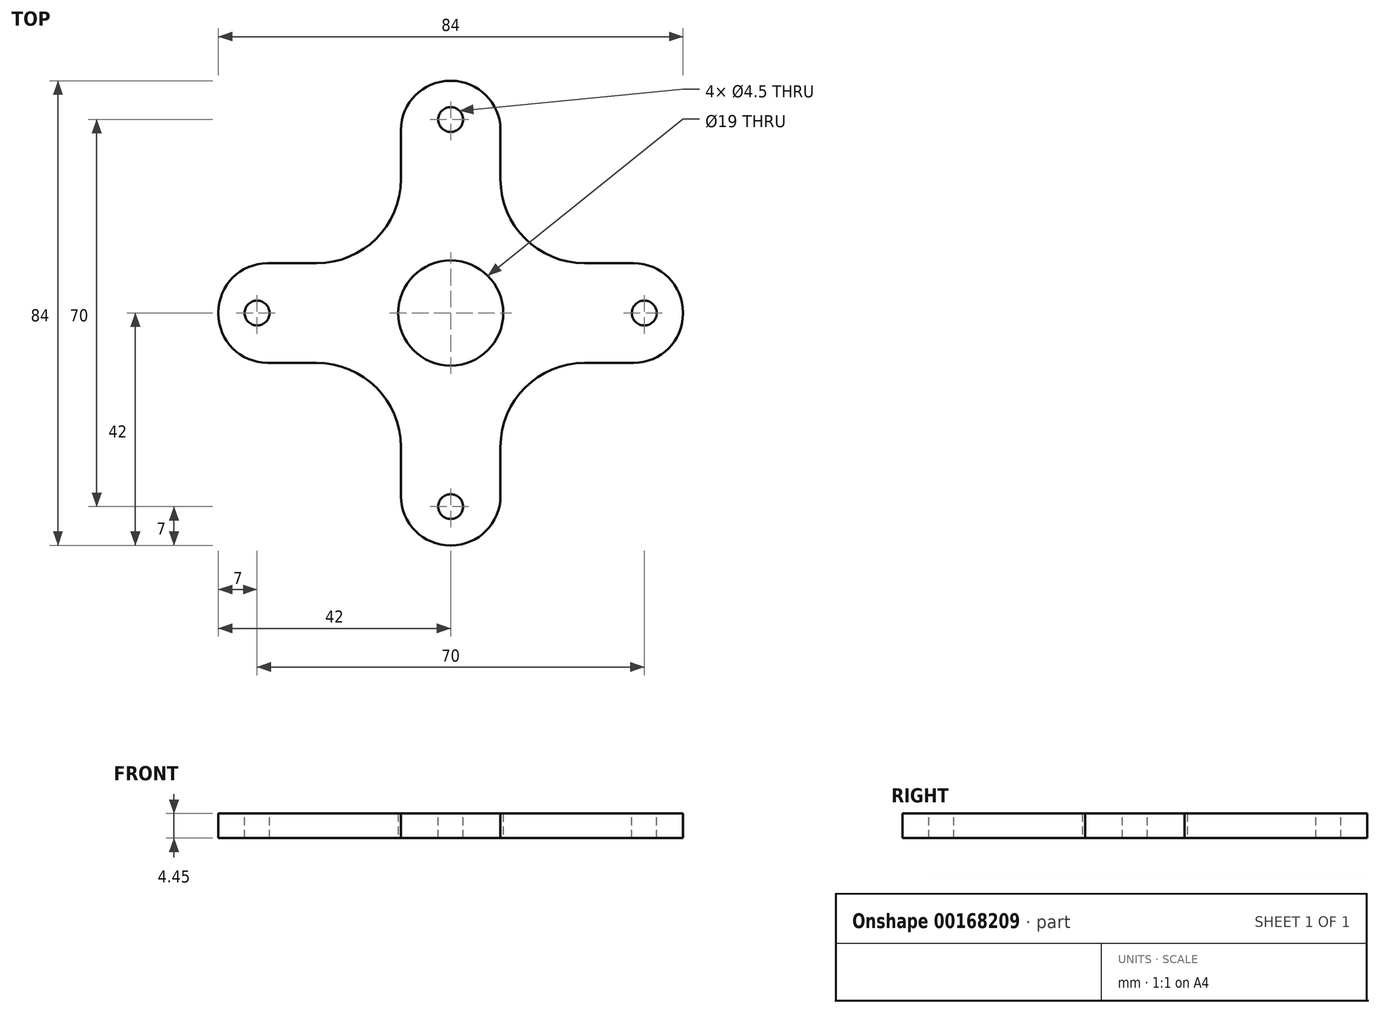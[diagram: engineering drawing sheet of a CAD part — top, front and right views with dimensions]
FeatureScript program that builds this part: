
annotation { "Feature Type Name" : "Feature", "Feature Type Description" : "" }
export const myFeature = defineFeature(function(context is Context, id is Id, definition is map)
    precondition{}
    {
        {
            var Q0;
            Q0=qCreatedBy(makeId("Top.planeOp"),FACE);
            var sketch = newSketch(context, id + "F0", { "sketchPlane" : qUnion([Q0])});
            skLineSegment(sketch, "E0.bottom", {"start": v(42, -9) * mm, "end": v(-42, -9) * mm});
            skLineSegment(sketch, "E0.top", {"start": v(42, 9) * mm, "end": v(-42, 9) * mm});
            skLineSegment(sketch, "E0.left", {"start": v(42, -9) * mm, "end": v(42, 9) * mm});
            skLineSegment(sketch, "E0.right", {"start": v(-42, -9) * mm, "end": v(-42, 9) * mm});
            skPoint(sketch, "E0.middle", {"position": v(0, 0) * mm});
            skSolve(sketch);
        }
        {
            var Q0;
            Q0=qSketchRegion(id+"F0",true);
            extrude(context, id + "F1", {"entities" : qUnion([Q0]), "depth" : 4.44 * mm});
        }
        {
            var Q0;
            Q0=qCreatedBy(makeId("Top.planeOp"),FACE);
            var sketch = newSketch(context, id + "F2", { "sketchPlane" : qUnion([Q0])});
            skLineSegment(sketch, "E1.bottom", {"start": v(9, -42) * mm, "end": v(-9, -42) * mm});
            skLineSegment(sketch, "E1.top", {"start": v(9, 42) * mm, "end": v(-9, 42) * mm});
            skLineSegment(sketch, "E1.left", {"start": v(9, -42) * mm, "end": v(9, 42) * mm});
            skLineSegment(sketch, "E1.right", {"start": v(-9, -42) * mm, "end": v(-9, 42) * mm});
            skPoint(sketch, "E1.middle", {"position": v(0, 0) * mm});
            skSolve(sketch);
        }
        {
            var Q0;
            Q0=qSketchRegion(id+"F2",true);
            var Q1;
            Q1=makeQuery(id+"F1.opExtrude","CAP_FACE",FACE,{"disambiguationData":[OSD([sQuery(id+"F0.wireOp",EDGE,"E0.bottom"),sQuery(id+"F0.wireOp",EDGE,"E0.top"),sQuery(id+"F0.wireOp",EDGE,"E0.left"),sQuery(id+"F0.wireOp",EDGE,"E0.right")])],"isStart":false});
            extrude(context, id + "F3", {"entities" : qUnion([Q0]), "operationType" : NewBodyOperationType.ADD, "endBound" : BoundingType.UP_TO_SURFACE, "endBoundEntityFace" : qUnion([Q1]), "depth" : 25.4 * mm});
        }
        {
            var Q0;
            Q0=makeQuery(id+"F3.opExtrude","SWEPT_EDGE",EDGE,{"disambiguationData":[OSD([sQuery(id+"F2.wireOp",EDGE,"E1.bottom"),sQuery(id+"F2.wireOp",EDGE,"E1.left")])]});
            var Q1;
            Q1=makeQuery(id+"F3.opExtrude","SWEPT_EDGE",EDGE,{"disambiguationData":[OSD([sQuery(id+"F2.wireOp",EDGE,"E1.bottom"),sQuery(id+"F2.wireOp",EDGE,"E1.right")])]});
            var Q2;
            Q2=makeQuery(id+"F1.opExtrude","SWEPT_EDGE",EDGE,{"disambiguationData":[OSD([sQuery(id+"F0.wireOp",EDGE,"E0.bottom"),sQuery(id+"F0.wireOp",EDGE,"E0.left")])]});
            var Q3;
            Q3=makeQuery(id+"F1.opExtrude","SWEPT_EDGE",EDGE,{"disambiguationData":[OSD([sQuery(id+"F0.wireOp",EDGE,"E0.top"),sQuery(id+"F0.wireOp",EDGE,"E0.left")])]});
            var Q4;
            Q4=makeQuery(id+"F3.opExtrude","SWEPT_EDGE",EDGE,{"disambiguationData":[OSD([sQuery(id+"F2.wireOp",EDGE,"E1.top"),sQuery(id+"F2.wireOp",EDGE,"E1.left")])]});
            var Q5;
            Q5=makeQuery(id+"F1.opExtrude","SWEPT_EDGE",EDGE,{"disambiguationData":[OSD([sQuery(id+"F0.wireOp",EDGE,"E0.bottom"),sQuery(id+"F0.wireOp",EDGE,"E0.right")])]});
            var Q6;
            Q6=makeQuery(id+"F1.opExtrude","SWEPT_EDGE",EDGE,{"disambiguationData":[OSD([sQuery(id+"F0.wireOp",EDGE,"E0.top"),sQuery(id+"F0.wireOp",EDGE,"E0.right")])]});
            var Q7;
            Q7=makeQuery(id+"F3.opExtrude","SWEPT_EDGE",EDGE,{"disambiguationData":[OSD([sQuery(id+"F2.wireOp",EDGE,"E1.top"),sQuery(id+"F2.wireOp",EDGE,"E1.right")])]});
            fillet(context, id + "F4", {"entities" : qUnion([Q0, Q1, Q2, Q3, Q4, Q5, Q6, Q7]), "radius" : 8.9 * mm, "tangentPropagation" : true, "allowEdgeOverflow" : false});
        }
        {
            var Q0;
            Q0=makeQuery(id+"F3.boolean.opBoolean","MERGE",FACE,{"derivedFrom":[makeQuery(id+"F1.opExtrude","CAP_FACE",FACE,{"disambiguationData":[OSD([sQuery(id+"F0.wireOp",EDGE,"E0.bottom"),sQuery(id+"F0.wireOp",EDGE,"E0.top"),sQuery(id+"F0.wireOp",EDGE,"E0.left"),sQuery(id+"F0.wireOp",EDGE,"E0.right")])],"isStart":false}),makeQuery(id+"F3.opExtrude","CAP_FACE",FACE,{"disambiguationData":[OSD([sQuery(id+"F2.wireOp",EDGE,"E1.bottom"),sQuery(id+"F2.wireOp",EDGE,"E1.top"),sQuery(id+"F2.wireOp",EDGE,"E1.left"),sQuery(id+"F2.wireOp",EDGE,"E1.right")])],"isStart":false})]});
            var sketch = newSketch(context, id + "F5", { "sketchPlane" : qUnion([Q0])});
            skPoint(sketch, "E2", {"position": v(35, 0) * mm});
            skLineSegment(sketch, "E3", {"start": v(0, 0) * mm, "end": v(35, 0) * mm, "construction": true});
            skPoint(sketch, "E4.1.0", {"position": v(0, 35) * mm});
            skPoint(sketch, "E4.2.0", {"position": v(-35, 0) * mm});
            skPoint(sketch, "E4.3.0", {"position": v(0, -35) * mm});
            skPoint(sketch, "E4.center", {"position": v(0, 0) * mm});
            skSolve(sketch);
        }
        {
            var Q0;
            Q0=sQuery(id+"F5.wireOp",VERTEX,"E2");
            var Q1;
            Q1=sQuery(id+"F5.wireOp",VERTEX,"E4.3.0");
            var Q2;
            Q2=sQuery(id+"F5.wireOp",VERTEX,"E4.2.0");
            var Q3;
            Q3=sQuery(id+"F5.wireOp",VERTEX,"E4.1.0");
            var Q4;
            Q4=makeQuery(id+"F1.opExtrude","SWEPT_BODY",BODY,{"disambiguationData":[OSD([sQuery(id+"F0.wireOp",EDGE,"E0.bottom"),sQuery(id+"F0.wireOp",EDGE,"E0.top"),sQuery(id+"F0.wireOp",EDGE,"E0.left"),sQuery(id+"F0.wireOp",EDGE,"E0.right")])]});
            hole(context, id + "F6", {"style" : HoleStyle.SIMPLE, "endStyle" : HoleEndStyle.THROUGH, "standardTappedOrClearance" : lookupTablePath({ "standard" : "ANSI", "fit" : "Normal (ASME)", "size" : "#8", "type" : "Clearance" }), "standardBlindInLast" : lookupTablePath({ "fit" : "Free", "standard" : "ANSI", "size" : "#8", "type" : "Clearance" }), "holeDiameter" : 4.5 * mm, "locations" : qUnion([Q0, Q1, Q2, Q3]), "scope" : qUnion([Q4]), "isTappedThrough" : true});
        }
        {
            var Q0;
            Q0=qCreatedBy(makeId("Top.planeOp"),FACE);
            var sketch = newSketch(context, id + "F7", { "sketchPlane" : qUnion([Q0])});
            skCircle(sketch, "E5", {"center": v(0, 0) * mm, "radius": 9.5 * mm});
            skSolve(sketch);
        }
        {
            var Q0;
            Q0=makeQuery(id+"F7.imprint","IMPRINT",FACE,{"disambiguationData":[TD([[makeQuery(id+"F7.imprint","IMPRINT",EDGE,{"derivedFrom":sQuery(id+"F7.wireOp",EDGE,"E5")}),1.0]])]});
            extrude(context, id + "F8", {"entities" : qUnion([Q0]), "operationType" : NewBodyOperationType.REMOVE, "endBound" : BoundingType.THROUGH_ALL, "depth" : 25.4 * mm});
        }
        {
            var Q0;
            Q0=makeQuery(id+"F3.boolean.opBoolean","INTERSECT",EDGE,{"derivedFrom":[makeQuery(id+"F1.opExtrude","SWEPT_FACE",FACE,{"disambiguationData":[OSD([sQuery(id+"F0.wireOp",EDGE,"E0.top")])]}),makeQuery(id+"F3.opExtrude","SWEPT_FACE",FACE,{"disambiguationData":[OSD([sQuery(id+"F2.wireOp",EDGE,"E1.left")])]})]});
            var Q1;
            Q1=makeQuery(id+"F3.boolean.opBoolean","INTERSECT",EDGE,{"derivedFrom":[makeQuery(id+"F1.opExtrude","SWEPT_FACE",FACE,{"disambiguationData":[OSD([sQuery(id+"F0.wireOp",EDGE,"E0.bottom")])]}),makeQuery(id+"F3.opExtrude","SWEPT_FACE",FACE,{"disambiguationData":[OSD([sQuery(id+"F2.wireOp",EDGE,"E1.left")])]})]});
            var Q2;
            Q2=makeQuery(id+"F3.boolean.opBoolean","INTERSECT",EDGE,{"derivedFrom":[makeQuery(id+"F1.opExtrude","SWEPT_FACE",FACE,{"disambiguationData":[OSD([sQuery(id+"F0.wireOp",EDGE,"E0.bottom")])]}),makeQuery(id+"F3.opExtrude","SWEPT_FACE",FACE,{"disambiguationData":[OSD([sQuery(id+"F2.wireOp",EDGE,"E1.right")])]})]});
            var Q3;
            Q3=makeQuery(id+"F3.boolean.opBoolean","INTERSECT",EDGE,{"derivedFrom":[makeQuery(id+"F1.opExtrude","SWEPT_FACE",FACE,{"disambiguationData":[OSD([sQuery(id+"F0.wireOp",EDGE,"E0.top")])]}),makeQuery(id+"F3.opExtrude","SWEPT_FACE",FACE,{"disambiguationData":[OSD([sQuery(id+"F2.wireOp",EDGE,"E1.right")])]})]});
            fillet(context, id + "F9", {"entities" : qUnion([Q0, Q1, Q2, Q3]), "radius" : 15.24 * mm, "tangentPropagation" : true, "allowEdgeOverflow" : false});
        }
    });
